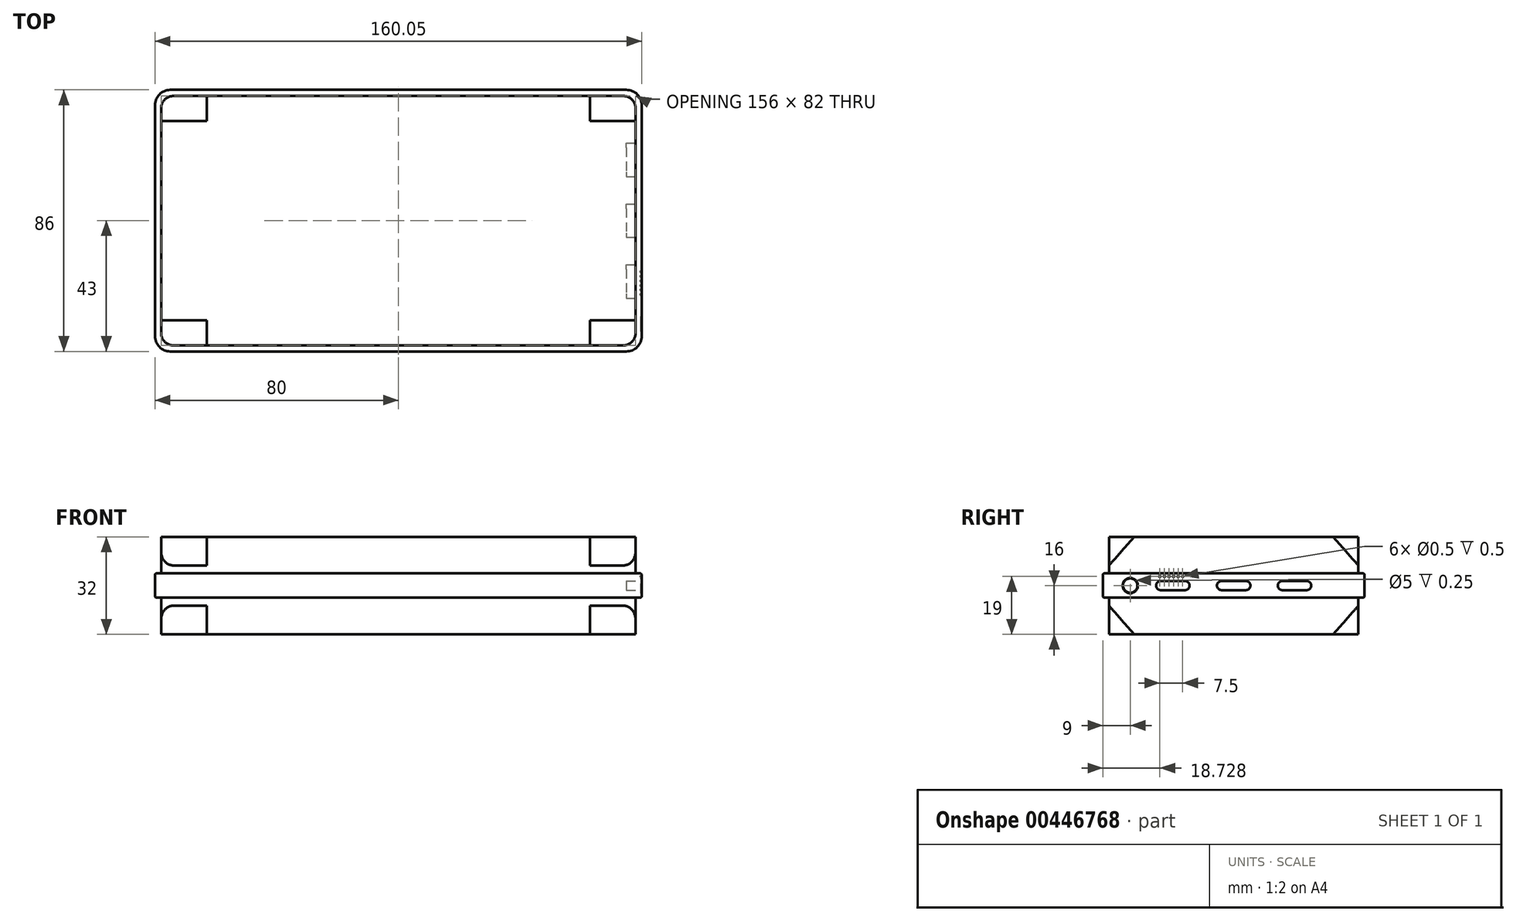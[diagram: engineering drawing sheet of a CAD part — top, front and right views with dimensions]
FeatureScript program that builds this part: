
annotation { "Feature Type Name" : "Feature", "Feature Type Description" : "" }
export const myFeature = defineFeature(function(context is Context, id is Id, definition is map)
    precondition{}
    {
        {
            var Q0;
            Q0=qCreatedBy(makeId("Top.planeOp"),FACE);
            var sketch = newSketch(context, id + "F0", { "sketchPlane" : qUnion([Q0])});
            skLineSegment(sketch, "E0.bottom", {"start": v(0, 43) * mm, "end": v(80, 43) * mm});
            skLineSegment(sketch, "E0.top", {"start": v(0, 0) * mm, "end": v(80, 0) * mm});
            skLineSegment(sketch, "E0.left", {"start": v(0, 43) * mm, "end": v(0, 0) * mm});
            skLineSegment(sketch, "E0.right", {"start": v(80, 43) * mm, "end": v(80, 0) * mm});
            skSolve(sketch);
        }
        {
            var Q0;
            Q0=makeQuery(id+"F0.imprint","IMPRINT",FACE,{"disambiguationData":[TD([[makeQuery(id+"F0.imprint","IMPRINT",EDGE,{"derivedFrom":sQuery(id+"F0.wireOp",EDGE,"E0.bottom")}),-1.0]])]});
            var Q1;
            Q1=makeQuery(id+"F0.imprint","IMPRINT",FACE,{"disambiguationData":[TD([[makeQuery(id+"F0.imprint","IMPRINT",EDGE,{"derivedFrom":sQuery(id+"F0.wireOp",EDGE,"E0.top")}),-1.0]])]});
            extrude(context, id + "F1", {"entities" : qUnion([Q0, Q1]), "depth" : 4 * mm});
        }
        {
            var Q0;
            Q0=makeQuery(id+"F1.opExtrude","CAP_FACE",FACE,{"disambiguationData":[OSD([sQuery(id+"F0.wireOp",EDGE,"E0.bottom"),sQuery(id+"F0.wireOp",EDGE,"E0.top"),sQuery(id+"F0.wireOp",EDGE,"E0.left"),sQuery(id+"F0.wireOp",EDGE,"E0.right")])],"isStart":false});
            var sketch = newSketch(context, id + "F2", { "sketchPlane" : qUnion([Q0])});
            skLineSegment(sketch, "E1.bottom", {"start": v(0, 0) * mm, "end": v(78, 0) * mm});
            skLineSegment(sketch, "E1.top", {"start": v(0, 41) * mm, "end": v(78, 41) * mm});
            skLineSegment(sketch, "E1.left", {"start": v(0, 0) * mm, "end": v(0, 41) * mm});
            skLineSegment(sketch, "E1.right", {"start": v(78, 0) * mm, "end": v(78, 41) * mm});
            skSolve(sketch);
        }
        {
            var Q0;
            Q0=makeQuery(id+"F2.imprint","IMPRINT",FACE,{"disambiguationData":[TD([[makeQuery(id+"F2.imprint","IMPRINT",EDGE,{"derivedFrom":sQuery(id+"F2.wireOp",EDGE,"E1.bottom")}),1.0]])]});
            extrude(context, id + "F3", {"entities" : qUnion([Q0]), "operationType" : NewBodyOperationType.ADD, "depth" : 12 * mm});
        }
        {
            var Q0;
            Q0=makeQuery(id+"F1.opExtrude","SWEPT_EDGE",EDGE,{"disambiguationData":[OSD([sQuery(id+"F0.wireOp",EDGE,"E0.bottom"),sQuery(id+"F0.wireOp",EDGE,"E0.right")])]});
            fillet(context, id + "F4", {"entities" : qUnion([Q0]), "radius" : 5 * mm, "tangentPropagation" : true, "allowEdgeOverflow" : false});
        }
        {
            var Q0;
            Q0=makeQuery(id+"F1.opExtrude","CAP_EDGE",EDGE,{"disambiguationData":[OSD([sQuery(id+"F0.wireOp",EDGE,"E0.bottom")])],"isStart":false});
            var Q1;
            {var subQ0=sQuery(id+"F0.wireOp",EDGE,"E0.right");var subQ1=sQuery(id+"F0.wireOp",EDGE,"E0.bottom");Q1=makeQuery(id+"F4.opFillet","BLEND_EDGE",EDGE,{"blendedFrom":[makeQuery(id+"F1.opExtrude","SWEPT_EDGE",EDGE,{"disambiguationData":[OSD([subQ1,subQ0])]}),makeQuery(id+"F1.opExtrude","CAP_FACE",FACE,{"disambiguationData":[OSD([subQ1,sQuery(id+"F0.wireOp",EDGE,"E0.top"),sQuery(id+"F0.wireOp",EDGE,"E0.left"),subQ0])],"isStart":false})],"blendedInto":[makeQuery(id+"F1.opExtrude","CAP_FACE",FACE,{"disambiguationData":[OSD([subQ1,sQuery(id+"F0.wireOp",EDGE,"E0.top"),sQuery(id+"F0.wireOp",EDGE,"E0.left"),subQ0])],"isStart":false})]});}
            var Q2;
            Q2=makeQuery(id+"F1.opExtrude","CAP_EDGE",EDGE,{"disambiguationData":[OSD([sQuery(id+"F0.wireOp",EDGE,"E0.right")])],"isStart":false});
            fillet(context, id + "F5", {"entities" : qUnion([Q0, Q1, Q2]), "radius" : 0.5 * mm, "tangentPropagation" : true, "allowEdgeOverflow" : false});
        }
        {
            var Q0;
            Q0=makeQuery(id+"F3.opExtrude","SWEPT_FACE",FACE,{"disambiguationData":[OSD([sQuery(id+"F2.wireOp",EDGE,"E1.right")])]});
            var sketch = newSketch(context, id + "F6", { "sketchPlane" : qUnion([Q0])});
            skLineSegment(sketch, "E2.0", {"start": v(0, 16) * mm, "end": v(41, 16) * mm});
            skLineSegment(sketch, "E3.0", {"start": v(41, 16) * mm, "end": v(41, 4) * mm});
            skLineSegment(sketch, "E4.0.3", {"start": v(41, 16) * mm, "end": v(0, 16) * mm});
            skLineSegment(sketch, "E5.0.1", {"start": v(41, 4) * mm, "end": v(41, 16) * mm});
            skLineSegment(sketch, "E6.0.0", {"start": v(0, 4) * mm, "end": v(41, 4) * mm});
            skLineSegment(sketch, "E6.0.3", {"start": v(0, 16) * mm, "end": v(0, 4) * mm});
            skLineSegment(sketch, "E7", {"start": v(32.73, 16) * mm, "end": v(41, 6.62) * mm});
            skSolve(sketch);
        }
        {
            var Q0;
            {var subQ3=sQuery(id+"F6.wireOp",EDGE,"E7");Q0=makeQuery(id+"F6.imprint","IMPRINT",FACE,{"disambiguationData":[TD([[makeQuery(id+"F6.imprint","IMPRINT",EDGE,{"derivedFrom":subQ3}),1.0]])]});}
            extrude(context, id + "F7", {"entities" : qUnion([Q0]), "operationType" : NewBodyOperationType.REMOVE, "oppositeDirection" : true, "depth" : 15 * mm});
        }
        {
            var Q0;
            Q0=makeQuery(id+"F3.opExtrude","SWEPT_EDGE",EDGE,{"disambiguationData":[OSD([sQuery(id+"F2.wireOp",EDGE,"E1.top"),sQuery(id+"F2.wireOp",EDGE,"E1.right")])]});
            fillet(context, id + "F8", {"entities" : qUnion([Q0]), "radius" : 4 * mm, "tangentPropagation" : true, "allowEdgeOverflow" : false});
        }
        {
            var Q0;
            Q0=makeQuery(id+"F1.opExtrude","SWEPT_BODY",BODY,{"disambiguationData":[OSD([sQuery(id+"F0.wireOp",EDGE,"E0.bottom"),sQuery(id+"F0.wireOp",EDGE,"E0.top"),sQuery(id+"F0.wireOp",EDGE,"E0.left"),sQuery(id+"F0.wireOp",EDGE,"E0.right")])]});
            var Q1;
            Q1=makeQuery(id+"F3.boolean.opBoolean","MERGE",FACE,{"derivedFrom":[makeQuery(id+"F1.opExtrude","SWEPT_FACE",FACE,{"disambiguationData":[OSD([sQuery(id+"F0.wireOp",EDGE,"E0.top")])]}),makeQuery(id+"F3.opExtrude","SWEPT_FACE",FACE,{"disambiguationData":[OSD([sQuery(id+"F2.wireOp",EDGE,"E1.bottom")])]})]});
            mirror(context, id + "F9", {"operationType" : NewBodyOperationType.ADD, "entities" : qUnion([Q0]), "mirrorPlane" : qUnion([Q1])});
        }
        {
            var Q0;
            Q0=makeQuery(id+"F1.opExtrude","SWEPT_BODY",BODY,{"disambiguationData":[OSD([sQuery(id+"F0.wireOp",EDGE,"E0.bottom"),sQuery(id+"F0.wireOp",EDGE,"E0.top"),sQuery(id+"F0.wireOp",EDGE,"E0.left"),sQuery(id+"F0.wireOp",EDGE,"E0.right")])]});
            var Q1;
            {var subQ0=makeQuery(id+"F3.boolean.opBoolean","MERGE",FACE,{"derivedFrom":[makeQuery(id+"F1.opExtrude","SWEPT_FACE",FACE,{"disambiguationData":[OSD([sQuery(id+"F0.wireOp",EDGE,"E0.left")])]}),makeQuery(id+"F3.opExtrude","SWEPT_FACE",FACE,{"disambiguationData":[OSD([sQuery(id+"F2.wireOp",EDGE,"E1.left")])]})]});Q1=makeQuery(id+"F9.boolean.opBoolean","MERGE",FACE,{"derivedFrom":[subQ0,makeQuery(id+"F9.opPattern","COPY",FACE,{"derivedFrom":subQ0,"instanceName":"1"})]});}
            mirror(context, id + "F10", {"operationType" : NewBodyOperationType.ADD, "entities" : qUnion([Q0]), "mirrorPlane" : qUnion([Q1])});
        }
        {
            var Q0;
            Q0=makeQuery(id+"F1.opExtrude","SWEPT_BODY",BODY,{"disambiguationData":[OSD([sQuery(id+"F0.wireOp",EDGE,"E0.bottom"),sQuery(id+"F0.wireOp",EDGE,"E0.top"),sQuery(id+"F0.wireOp",EDGE,"E0.left"),sQuery(id+"F0.wireOp",EDGE,"E0.right")])]});
            var Q1;
            {var subQ0=makeQuery(id+"F1.opExtrude","CAP_FACE",FACE,{"disambiguationData":[OSD([sQuery(id+"F0.wireOp",EDGE,"E0.bottom"),sQuery(id+"F0.wireOp",EDGE,"E0.top"),sQuery(id+"F0.wireOp",EDGE,"E0.left"),sQuery(id+"F0.wireOp",EDGE,"E0.right")])],"isStart":true});var subQ1=makeQuery(id+"F9.boolean.opBoolean","MERGE",FACE,{"derivedFrom":[subQ0,makeQuery(id+"F9.opPattern","COPY",FACE,{"derivedFrom":subQ0,"instanceName":"1"})]});Q1=makeQuery(id+"F10.boolean.opBoolean","MERGE",FACE,{"derivedFrom":[subQ1,makeQuery(id+"F10.opPattern","COPY",FACE,{"derivedFrom":subQ1,"instanceName":"1"})]});}
            mirror(context, id + "F11", {"operationType" : NewBodyOperationType.ADD, "entities" : qUnion([Q0]), "mirrorPlane" : qUnion([Q1])});
        }
        {
            var Q0;
            {var subQ0=makeQuery(id+"F1.opExtrude","SWEPT_FACE",FACE,{"disambiguationData":[OSD([sQuery(id+"F0.wireOp",EDGE,"E0.right")])]});var subQ1=makeQuery(id+"F9.boolean.opBoolean","MERGE",FACE,{"derivedFrom":[subQ0,makeQuery(id+"F9.opPattern","COPY",FACE,{"derivedFrom":subQ0,"instanceName":"1"})]});Q0=makeQuery(id+"F11.boolean.opBoolean","MERGE",FACE,{"derivedFrom":[subQ1,makeQuery(id+"F11.opPattern","COPY",FACE,{"derivedFrom":subQ1,"instanceName":"1"})]});}
            var sketch = newSketch(context, id + "F12", { "sketchPlane" : qUnion([Q0])});
            skLineSegment(sketch, "E8.bottom", {"start": v(4, -1.5) * mm, "end": v(-4, -1.5) * mm});
            skLineSegment(sketch, "E8.top", {"start": v(4, 1.5) * mm, "end": v(-4, 1.5) * mm});
            skPoint(sketch, "E8.middle", {"position": v(0, 0) * mm});
            skArc(sketch, "E9", {"start": v(-4, 1.5) * mm, "mid": v(-5.5, 0) * mm, "end": v(-4, -1.5) * mm});
            skArc(sketch, "E10", {"start": v(4, -1.5) * mm, "mid": v(5.5, 0) * mm, "end": v(4, 1.5) * mm});
            skLineSegment(sketch, "E11.bottom", {"start": v(24, -1.5) * mm, "end": v(16, -1.5) * mm});
            skLineSegment(sketch, "E11.top", {"start": v(24, 1.5) * mm, "end": v(16, 1.5) * mm});
            skArc(sketch, "E12", {"start": v(16, 1.5) * mm, "mid": v(14.5, 0) * mm, "end": v(16, -1.5) * mm});
            skArc(sketch, "E13", {"start": v(24, -1.5) * mm, "mid": v(25.5, 0) * mm, "end": v(24, 1.5) * mm});
            skLineSegment(sketch, "E14.bottom", {"start": v(-16, -1.5) * mm, "end": v(-24, -1.5) * mm});
            skLineSegment(sketch, "E14.top", {"start": v(-16, 1.5) * mm, "end": v(-24, 1.5) * mm});
            skArc(sketch, "E15", {"start": v(-24, 1.5) * mm, "mid": v(-25.5, 0) * mm, "end": v(-24, -1.5) * mm});
            skArc(sketch, "E16", {"start": v(-16, -1.5) * mm, "mid": v(-14.5, 0) * mm, "end": v(-16, 1.5) * mm});
            skCircle(sketch, "E17", {"center": v(-34, 0) * mm, "radius": 2.5 * mm});
            skSolve(sketch);
        }
        {
            var Q0;
            Q0=makeQuery(id+"F12.imprint","IMPRINT",FACE,{"disambiguationData":[TD([[makeQuery(id+"F12.imprint","IMPRINT",EDGE,{"derivedFrom":sQuery(id+"F12.wireOp",EDGE,"E17")}),1.0]])]});
            extrude(context, id + "F13", {"entities" : qUnion([Q0]), "operationType" : NewBodyOperationType.REMOVE, "oppositeDirection" : true, "depth" : 0.25 * mm});
        }
        {
            var Q0;
            Q0=makeQuery(id+"F12.imprint","IMPRINT",FACE,{"disambiguationData":[TD([[makeQuery(id+"F12.imprint","IMPRINT",EDGE,{"derivedFrom":sQuery(id+"F12.wireOp",EDGE,"E14.bottom")}),-1.0]])]});
            var Q1;
            Q1=makeQuery(id+"F12.imprint","IMPRINT",FACE,{"disambiguationData":[TD([[makeQuery(id+"F12.imprint","IMPRINT",EDGE,{"derivedFrom":sQuery(id+"F12.wireOp",EDGE,"E8.bottom")}),-1.0]])]});
            var Q2;
            Q2=makeQuery(id+"F12.imprint","IMPRINT",FACE,{"disambiguationData":[TD([[makeQuery(id+"F12.imprint","IMPRINT",EDGE,{"derivedFrom":sQuery(id+"F12.wireOp",EDGE,"E11.bottom")}),-1.0]])]});
            extrude(context, id + "F14", {"entities" : qUnion([Q0, Q1, Q2]), "operationType" : NewBodyOperationType.REMOVE, "oppositeDirection" : true, "depth" : 5 * mm});
        }
        {
            var Q0;
            Q0=makeQuery(id+"F13.boolean.opBoolean","COPY",FACE,{"derivedFrom":makeQuery(id+"F13.opExtrude","CAP_FACE",FACE,{"disambiguationData":[OSD([sQuery(id+"F12.wireOp",EDGE,"E17")])],"isStart":false})});
            var sketch = newSketch(context, id + "F15", { "sketchPlane" : qUnion([Q0])});
            skCircle(sketch, "E18", {"center": v(-34, 0) * mm, "radius": 2.38 * mm});
            skSolve(sketch);
        }
        {
            var Q0;
            Q0=makeQuery(id+"F15.imprint","IMPRINT",FACE,{"disambiguationData":[TD([[makeQuery(id+"F15.imprint","IMPRINT",EDGE,{"derivedFrom":sQuery(id+"F15.wireOp",EDGE,"E18")}),1.0]])]});
            extrude(context, id + "F16", {"entities" : qUnion([Q0]), "operationType" : NewBodyOperationType.ADD, "depth" : 0.3 * mm});
        }
        {
            var Q0;
            {var subQ0=makeQuery(id+"F1.opExtrude","SWEPT_FACE",FACE,{"disambiguationData":[OSD([sQuery(id+"F0.wireOp",EDGE,"E0.right")])]});var subQ1=makeQuery(id+"F9.boolean.opBoolean","MERGE",FACE,{"derivedFrom":[subQ0,makeQuery(id+"F9.opPattern","COPY",FACE,{"derivedFrom":subQ0,"instanceName":"1"})]});Q0=makeQuery(id+"F11.boolean.opBoolean","MERGE",FACE,{"derivedFrom":[subQ1,makeQuery(id+"F11.opPattern","COPY",FACE,{"derivedFrom":subQ1,"instanceName":"1"})]});}
            var sketch = newSketch(context, id + "F17", { "sketchPlane" : qUnion([Q0])});
            skCircle(sketch, "E19", {"center": v(-21.27, 3) * mm, "radius": 0.25 * mm});
            skCircle(sketch, "E20", {"center": v(-18.27, 3) * mm, "radius": 0.25 * mm});
            skCircle(sketch, "E21", {"center": v(-16.77, 3) * mm, "radius": 0.25 * mm});
            skCircle(sketch, "E22", {"center": v(-22.77, 3) * mm, "radius": 0.25 * mm});
            skCircle(sketch, "E23", {"center": v(-24.27, 3) * mm, "radius": 0.25 * mm});
            skCircle(sketch, "E24", {"center": v(-19.77, 3) * mm, "radius": 0.25 * mm});
            skSolve(sketch);
        }
        {
            var Q0;
            Q0=qSketchRegion(id+"F17",true);
            extrude(context, id + "F18", {"entities" : qUnion([Q0]), "operationType" : NewBodyOperationType.REMOVE, "oppositeDirection" : true, "depth" : 0.5 * mm});
        }
    });
